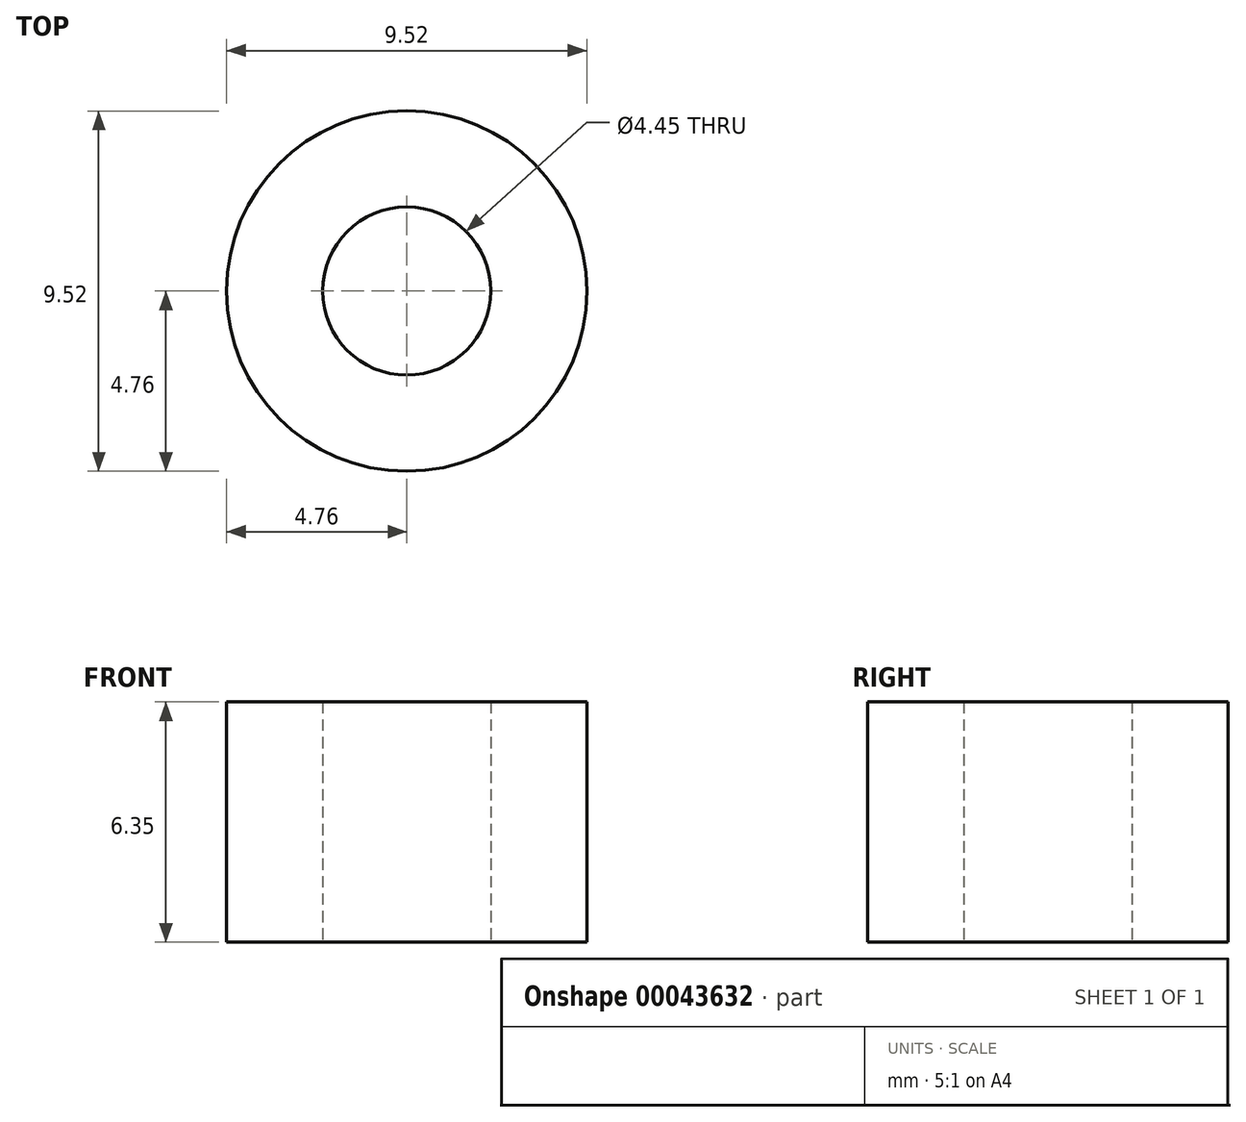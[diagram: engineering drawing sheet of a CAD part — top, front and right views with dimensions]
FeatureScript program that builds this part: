
annotation { "Feature Type Name" : "Feature", "Feature Type Description" : "" }
export const myFeature = defineFeature(function(context is Context, id is Id, definition is map)
    precondition{}
    {
        {
            var Q0;
            Q0=qCreatedBy(makeId("Top.planeOp"),FACE);
            var sketch = newSketch(context, id + "F0", { "sketchPlane" : qUnion([Q0])});
            skCircle(sketch, "E0", {"center": v(0, 0) * mm, "radius": 4.76 * mm});
            skCircle(sketch, "E1", {"center": v(0, 0) * mm, "radius": 2.22 * mm});
            skSolve(sketch);
        }
        {
            var Q0;
            Q0=makeQuery(id+"F0.imprint","IMPRINT",FACE,{"disambiguationData":[TD([[makeQuery(id+"F0.imprint","IMPRINT",EDGE,{"derivedFrom":sQuery(id+"F0.wireOp",EDGE,"E0")}),1.0]])]});
            extrude(context, id + "F1", {"entities" : qUnion([Q0]), "depth" : 6.35 * mm});
        }
    });
